# Revit family: Series_500_XX_Standard
name_source: partatom
category: Windows
revit_build: Autodesk Revit 2014 (Build: 20130308_1515(x64)
units: mm (PartAtom-declared; Revit-internal decimal feet)

## types (33) — shared parameters
Centered In Wall = Yes
Custom Sash Width Left = 600 mm
Default Sill Height = 800 mm
Description = 500 Slenderline Sliding Window
Equal Sash Width = Yes
Frame Thickness = 54 mm
Glass Type = Glass
Glazing Thickness = 4 mm  [stored 0.0131234 ft]
Heavy Duty Interlocker = No
Limit Sash Height Max = 1500 mm  [stored 4.92126 ft]
Limit Sash Height Min = 300 mm  [stored 0.984252 ft]
Limit Sash Width Max = 750 mm  [stored 2.46063 ft]
Limit Sash Width Min = 300 mm  [stored 0.984252 ft]
Limit Window Height Max = 1575 mm
Limit Window Height Min = 375 mm
Limit Window Width Max = 1531 mm  [stored 5.02297 ft]
Limit Window Width Min = 631 mm  [stored 2.07021 ft]
Manufacturer = Crealco
Model = 500 Slenderline Sliding Window
Rough Width = 3 mm  [stored 0.00984252 ft]
Sash Frame Seal = 1 mm  [stored 0.00328084 ft]
Standard Interlocker = Yes
Wall Closure = By host
zero-valued in all types: Custom Frame Offset From Exterior, Is Heavy Duty Interlocker

## per-type parameters (varying)
| type | Area Left Sash Glazing | Area Right Sash Glazing | Custom Windload | Custom Window Height | Custom Window Width | Height | Limit Sash Width Left Max | Limit Sash Width Left Min | Max Pane Area | Sash Height | Sash Width Left | Sash Width Right | Width | Windload Design |
| 500SW-0906XX-1000Pa | 0.18 m² | 0.18 m² | 1000 mm  [stored 3.28084 ft] | 590 mm  [stored 1.9357 ft] | 890 mm  [stored 2.91995 ft] | 590 mm  [stored 1.9357 ft] | 559 mm  [stored 1.83399 ft] | 300 mm  [stored 0.984252 ft] | 0.18 m² | 515 mm | 430 mm | 430 mm | 890 mm  [stored 2.91995 ft] | 1000 mm  [stored 3.28084 ft] |
| 500SW-0906XX-1500Pa | 0.18 m² | 0.18 m² | 1500 mm  [stored 4.92126 ft] | 590 mm  [stored 1.9357 ft] | 890 mm  [stored 2.91995 ft] | 590 mm  [stored 1.9357 ft] | 559 mm  [stored 1.83399 ft] | 300 mm  [stored 0.984252 ft] | 0.18 m² | 515 mm | 430 mm | 430 mm | 890 mm  [stored 2.91995 ft] | 1500 mm  [stored 4.92126 ft] |
| 500SW-0906XX-2000Pa | 0.18 m² | 0.18 m² | 2000 mm  [stored 6.56168 ft] | 590 mm  [stored 1.9357 ft] | 890 mm  [stored 2.91995 ft] | 590 mm  [stored 1.9357 ft] | 559 mm  [stored 1.83399 ft] | 300 mm  [stored 0.984252 ft] | 0.18 m² | 515 mm | 430 mm | 430 mm | 890 mm  [stored 2.91995 ft] | 2000 mm  [stored 6.56168 ft] |
| 500SW-1206XX-1000Pa | 0.24 m² | 0.24 m² | 1000 mm  [stored 3.28084 ft] | 590 mm  [stored 1.9357 ft] | 1190 mm  [stored 3.9042 ft] | 590 mm  [stored 1.9357 ft] | 750 mm  [stored 2.46063 ft] | 409 mm  [stored 1.34186 ft] | 0.24 m² | 515 mm | 580 mm | 580 mm | 1190 mm  [stored 3.9042 ft] | 1000 mm  [stored 3.28084 ft] |
| 500SW-1206XX-1500Pa | 0.24 m² | 0.24 m² | 1500 mm  [stored 4.92126 ft] | 590 mm  [stored 1.9357 ft] | 1190 mm  [stored 3.9042 ft] | 590 mm  [stored 1.9357 ft] | 750 mm  [stored 2.46063 ft] | 409 mm  [stored 1.34186 ft] | 0.24 m² | 515 mm | 580 mm | 580 mm | 1190 mm  [stored 3.9042 ft] | 1500 mm  [stored 4.92126 ft] |
| 500SW-1206XX-2000Pa | 0.24 m² | 0.24 m² | 2000 mm  [stored 6.56168 ft] | 590 mm  [stored 1.9357 ft] | 1190 mm  [stored 3.9042 ft] | 590 mm  [stored 1.9357 ft] | 750 mm  [stored 2.46063 ft] | 409 mm  [stored 1.34186 ft] | 0.24 m² | 515 mm | 580 mm | 580 mm | 1190 mm  [stored 3.9042 ft] | 2000 mm  [stored 6.56168 ft] |
| 500SW-1506XX-1000Pa | 0.31 m² | 0.31 m² | 1000 mm  [stored 3.28084 ft] | 590 mm  [stored 1.9357 ft] | 1490 mm  [stored 4.88845 ft] | 590 mm  [stored 1.9357 ft] | 750 mm  [stored 2.46063 ft] | 709 mm  [stored 2.32612 ft] | 0.31 m² | 515 mm | 730 mm | 730 mm | 1490 mm  [stored 4.88845 ft] | 1000 mm  [stored 3.28084 ft] |
| 500SW-1506XX-1500Pa | 0.31 m² | 0.31 m² | 1500 mm  [stored 4.92126 ft] | 590 mm  [stored 1.9357 ft] | 1490 mm  [stored 4.88845 ft] | 590 mm  [stored 1.9357 ft] | 750 mm  [stored 2.46063 ft] | 709 mm  [stored 2.32612 ft] | 0.31 m² | 515 mm | 730 mm | 730 mm | 1490 mm  [stored 4.88845 ft] | 1500 mm  [stored 4.92126 ft] |
| 500SW-1506XX-2000Pa | 0.31 m² | 0.31 m² | 2000 mm  [stored 6.56168 ft] | 590 mm  [stored 1.9357 ft] | 1490 mm  [stored 4.88845 ft] | 590 mm  [stored 1.9357 ft] | 750 mm  [stored 2.46063 ft] | 709 mm  [stored 2.32612 ft] | 0.31 m² | 515 mm | 730 mm | 730 mm | 1490 mm  [stored 4.88845 ft] | 2000 mm  [stored 6.56168 ft] |
| 500SW-0909XX-1000Pa | 0.3 m² | 0.3 m² | 1000 mm  [stored 3.28084 ft] | 890 mm  [stored 2.91995 ft] | 890 mm  [stored 2.91995 ft] | 890 mm  [stored 2.91995 ft] | 559 mm  [stored 1.83399 ft] | 300 mm  [stored 0.984252 ft] | 0.3 m² | 815 mm | 430 mm | 430 mm | 890 mm  [stored 2.91995 ft] | 1000 mm  [stored 3.28084 ft] |
| 500SW-0909XX-1500Pa | 0.3 m² | 0.3 m² | 1500 mm  [stored 4.92126 ft] | 890 mm  [stored 2.91995 ft] | 890 mm  [stored 2.91995 ft] | 890 mm  [stored 2.91995 ft] | 559 mm  [stored 1.83399 ft] | 300 mm  [stored 0.984252 ft] | 0.3 m² | 815 mm | 430 mm | 430 mm | 890 mm  [stored 2.91995 ft] | 1500 mm  [stored 4.92126 ft] |
| 500SW-0909XX-2000Pa | 0.3 m² | 0.3 m² | 2000 mm  [stored 6.56168 ft] | 890 mm  [stored 2.91995 ft] | 890 mm  [stored 2.91995 ft] | 890 mm  [stored 2.91995 ft] | 559 mm  [stored 1.83399 ft] | 300 mm  [stored 0.984252 ft] | 0.3 m² | 815 mm | 430 mm | 430 mm | 890 mm  [stored 2.91995 ft] | 2000 mm  [stored 6.56168 ft] |
| 500SW-1209XX-1000Pa | 0.41 m² | 0.41 m² | 1000 mm  [stored 3.28084 ft] | 890 mm  [stored 2.91995 ft] | 1190 mm  [stored 3.9042 ft] | 890 mm  [stored 2.91995 ft] | 750 mm  [stored 2.46063 ft] | 409 mm  [stored 1.34186 ft] | 0.41 m² | 815 mm | 580 mm | 580 mm | 1190 mm  [stored 3.9042 ft] | 1000 mm  [stored 3.28084 ft] |
| 500SW-1209XX-1500Pa | 0.41 m² | 0.41 m² | 1500 mm  [stored 4.92126 ft] | 890 mm  [stored 2.91995 ft] | 1190 mm  [stored 3.9042 ft] | 890 mm  [stored 2.91995 ft] | 750 mm  [stored 2.46063 ft] | 409 mm  [stored 1.34186 ft] | 0.41 m² | 815 mm | 580 mm | 580 mm | 1190 mm  [stored 3.9042 ft] | 1500 mm  [stored 4.92126 ft] |
| 500SW-1209XX-2000Pa | 0.41 m² | 0.41 m² | 2000 mm  [stored 6.56168 ft] | 890 mm  [stored 2.91995 ft] | 1190 mm  [stored 3.9042 ft] | 890 mm  [stored 2.91995 ft] | 750 mm  [stored 2.46063 ft] | 409 mm  [stored 1.34186 ft] | 0.41 m² | 815 mm | 580 mm | 580 mm | 1190 mm  [stored 3.9042 ft] | 2000 mm  [stored 6.56168 ft] |
| 500SW-1509XX-1000Pa | 0.52 m² | 0.52 m² | 1000 mm  [stored 3.28084 ft] | 890 mm  [stored 2.91995 ft] | 1490 mm  [stored 4.88845 ft] | 890 mm  [stored 2.91995 ft] | 750 mm  [stored 2.46063 ft] | 709 mm  [stored 2.32612 ft] | 0.52 m² | 815 mm | 730 mm | 730 mm | 1490 mm  [stored 4.88845 ft] | 1000 mm  [stored 3.28084 ft] |
| 500SW-1509XX-1500Pa | 0.52 m² | 0.52 m² | 1500 mm  [stored 4.92126 ft] | 890 mm  [stored 2.91995 ft] | 1490 mm  [stored 4.88845 ft] | 890 mm  [stored 2.91995 ft] | 750 mm  [stored 2.46063 ft] | 709 mm  [stored 2.32612 ft] | 0.52 m² | 815 mm | 730 mm | 730 mm | 1490 mm  [stored 4.88845 ft] | 1500 mm  [stored 4.92126 ft] |
| 500SW-1509XX-2000Pa | 0.52 m² | 0.52 m² | 2000 mm  [stored 6.56168 ft] | 890 mm  [stored 2.91995 ft] | 1490 mm  [stored 4.88845 ft] | 890 mm  [stored 2.91995 ft] | 750 mm  [stored 2.46063 ft] | 709 mm  [stored 2.32612 ft] | 0.52 m² | 815 mm | 730 mm | 730 mm | 1490 mm  [stored 4.88845 ft] | 2000 mm  [stored 6.56168 ft] |
| 500SW-0912XX-1000Pa | 0.42 m² | 0.42 m² | 1000 mm  [stored 3.28084 ft] | 1190 mm  [stored 3.9042 ft] | 890 mm  [stored 2.91995 ft] | 1190 mm  [stored 3.9042 ft] | 559 mm  [stored 1.83399 ft] | 300 mm  [stored 0.984252 ft] | 0.42 m² | 1115 mm | 430 mm | 430 mm | 890 mm  [stored 2.91995 ft] | 1000 mm  [stored 3.28084 ft] |
| 500SW-0912XX-1500Pa | 0.42 m² | 0.42 m² | 1500 mm  [stored 4.92126 ft] | 1190 mm  [stored 3.9042 ft] | 890 mm  [stored 2.91995 ft] | 1190 mm  [stored 3.9042 ft] | 559 mm  [stored 1.83399 ft] | 300 mm  [stored 0.984252 ft] | 0.42 m² | 1115 mm | 430 mm | 430 mm | 890 mm  [stored 2.91995 ft] | 1500 mm  [stored 4.92126 ft] |
| 500SW-0912XX-2000Pa | 0.42 m² | 0.42 m² | 2000 mm  [stored 6.56168 ft] | 1190 mm  [stored 3.9042 ft] | 890 mm  [stored 2.91995 ft] | 1190 mm  [stored 3.9042 ft] | 559 mm  [stored 1.83399 ft] | 300 mm  [stored 0.984252 ft] | 0.42 m² | 1115 mm | 430 mm | 430 mm | 890 mm  [stored 2.91995 ft] | 2000 mm  [stored 6.56168 ft] |
| 500SW-0915XX-1000Pa | 0.54 m² | 0.54 m² | 1000 mm  [stored 3.28084 ft] | 1490 mm  [stored 4.88845 ft] | 890 mm  [stored 2.91995 ft] | 1490 mm  [stored 4.88845 ft] | 559 mm  [stored 1.83399 ft] | 300 mm  [stored 0.984252 ft] | 0.54 m² | 1415 mm  [stored 4.64239 ft] | 430 mm | 430 mm | 890 mm  [stored 2.91995 ft] | 1000 mm  [stored 3.28084 ft] |
| 500SW-0915XX-1500Pa | 0.54 m² | 0.54 m² | 1500 mm  [stored 4.92126 ft] | 1490 mm  [stored 4.88845 ft] | 890 mm  [stored 2.91995 ft] | 1490 mm  [stored 4.88845 ft] | 559 mm  [stored 1.83399 ft] | 300 mm  [stored 0.984252 ft] | 0.54 m² | 1415 mm  [stored 4.64239 ft] | 430 mm | 430 mm | 890 mm  [stored 2.91995 ft] | 1500 mm  [stored 4.92126 ft] |
| 500SW-0915XX-2000Pa | 0.54 m² | 0.54 m² | 2000 mm  [stored 6.56168 ft] | 1490 mm  [stored 4.88845 ft] | 890 mm  [stored 2.91995 ft] | 1490 mm  [stored 4.88845 ft] | 559 mm  [stored 1.83399 ft] | 300 mm  [stored 0.984252 ft] | 0.54 m² | 1415 mm  [stored 4.64239 ft] | 430 mm | 430 mm | 890 mm  [stored 2.91995 ft] | 2000 mm  [stored 6.56168 ft] |
| 500SW-1215XX-1000Pa | 0.74 m² | 0.74 m² | 1000 mm  [stored 3.28084 ft] | 1490 mm  [stored 4.88845 ft] | 1190 mm  [stored 3.9042 ft] | 1490 mm  [stored 4.88845 ft] | 750 mm  [stored 2.46063 ft] | 409 mm  [stored 1.34186 ft] | 0.74 m² | 1415 mm  [stored 4.64239 ft] | 580 mm | 580 mm | 1190 mm  [stored 3.9042 ft] | 1000 mm  [stored 3.28084 ft] |
| 500SW-1215XX-1500Pa | 0.74 m² | 0.74 m² | 1500 mm  [stored 4.92126 ft] | 1490 mm  [stored 4.88845 ft] | 1190 mm  [stored 3.9042 ft] | 1490 mm  [stored 4.88845 ft] | 750 mm  [stored 2.46063 ft] | 409 mm  [stored 1.34186 ft] | 0.74 m² | 1415 mm  [stored 4.64239 ft] | 580 mm | 580 mm | 1190 mm  [stored 3.9042 ft] | 1500 mm  [stored 4.92126 ft] |
| 500SW-1515XX-1000Pa | 0.94 m² | 0.94 m² | 1000 mm  [stored 3.28084 ft] | 1490 mm  [stored 4.88845 ft] | 1490 mm  [stored 4.88845 ft] | 1490 mm  [stored 4.88845 ft] | 750 mm  [stored 2.46063 ft] | 709 mm  [stored 2.32612 ft] | 0.94 m² | 1415 mm  [stored 4.64239 ft] | 730 mm | 730 mm | 1490 mm  [stored 4.88845 ft] | 1000 mm  [stored 3.28084 ft] |
| 500SW-1212XX-1000Pa | 0.57 m² | 0.57 m² | 1000 mm  [stored 3.28084 ft] | 1190 mm  [stored 3.9042 ft] | 1190 mm  [stored 3.9042 ft] | 1190 mm  [stored 3.9042 ft] | 750 mm  [stored 2.46063 ft] | 409 mm  [stored 1.34186 ft] | 0.57 m² | 1115 mm | 580 mm | 580 mm | 1190 mm  [stored 3.9042 ft] | 1000 mm  [stored 3.28084 ft] |
| 500SW-1212XX-1500Pa | 0.57 m² | 0.57 m² | 1500 mm  [stored 4.92126 ft] | 1190 mm  [stored 3.9042 ft] | 1190 mm  [stored 3.9042 ft] | 1190 mm  [stored 3.9042 ft] | 750 mm  [stored 2.46063 ft] | 409 mm  [stored 1.34186 ft] | 0.57 m² | 1115 mm | 580 mm | 580 mm | 1190 mm  [stored 3.9042 ft] | 1500 mm  [stored 4.92126 ft] |
| 500SW-1212XX-2000Pa | 0.57 m² | 0.57 m² | 2000 mm  [stored 6.56168 ft] | 1190 mm  [stored 3.9042 ft] | 1190 mm  [stored 3.9042 ft] | 1190 mm  [stored 3.9042 ft] | 750 mm  [stored 2.46063 ft] | 409 mm  [stored 1.34186 ft] | 0.57 m² | 1115 mm | 580 mm | 580 mm | 1190 mm  [stored 3.9042 ft] | 2000 mm  [stored 6.56168 ft] |
| 500SW-1512XX-1000Pa | 0.73 m² | 0.73 m² | 1000 mm  [stored 3.28084 ft] | 1190 mm  [stored 3.9042 ft] | 1490 mm  [stored 4.88845 ft] | 1190 mm  [stored 3.9042 ft] | 750 mm  [stored 2.46063 ft] | 709 mm  [stored 2.32612 ft] | 0.73 m² | 1115 mm | 730 mm | 730 mm | 1490 mm  [stored 4.88845 ft] | 1000 mm  [stored 3.28084 ft] |
| 500SW-1512XX-1500Pa | 0.73 m² | 0.73 m² | 1500 mm  [stored 4.92126 ft] | 1190 mm  [stored 3.9042 ft] | 1490 mm  [stored 4.88845 ft] | 1190 mm  [stored 3.9042 ft] | 750 mm  [stored 2.46063 ft] | 709 mm  [stored 2.32612 ft] | 0.73 m² | 1115 mm | 730 mm | 730 mm | 1490 mm  [stored 4.88845 ft] | 1500 mm  [stored 4.92126 ft] |
| 500SW-1512XX-2000Pa | 0.73 m² | 0.73 m² | 2000 mm  [stored 6.56168 ft] | 1190 mm  [stored 3.9042 ft] | 1490 mm  [stored 4.88845 ft] | 1190 mm  [stored 3.9042 ft] | 750 mm  [stored 2.46063 ft] | 709 mm  [stored 2.32612 ft] | 0.73 m² | 1115 mm | 730 mm | 730 mm | 1490 mm  [stored 4.88845 ft] | 2000 mm  [stored 6.56168 ft] |

note: [stored X ft] marks values corroborated as IEEE doubles in the binary element streams (Revit-internal decimal feet)

## geometry (parser evidence)
native form markers: Sweep x46
no freeform markers — native parametric forms only
